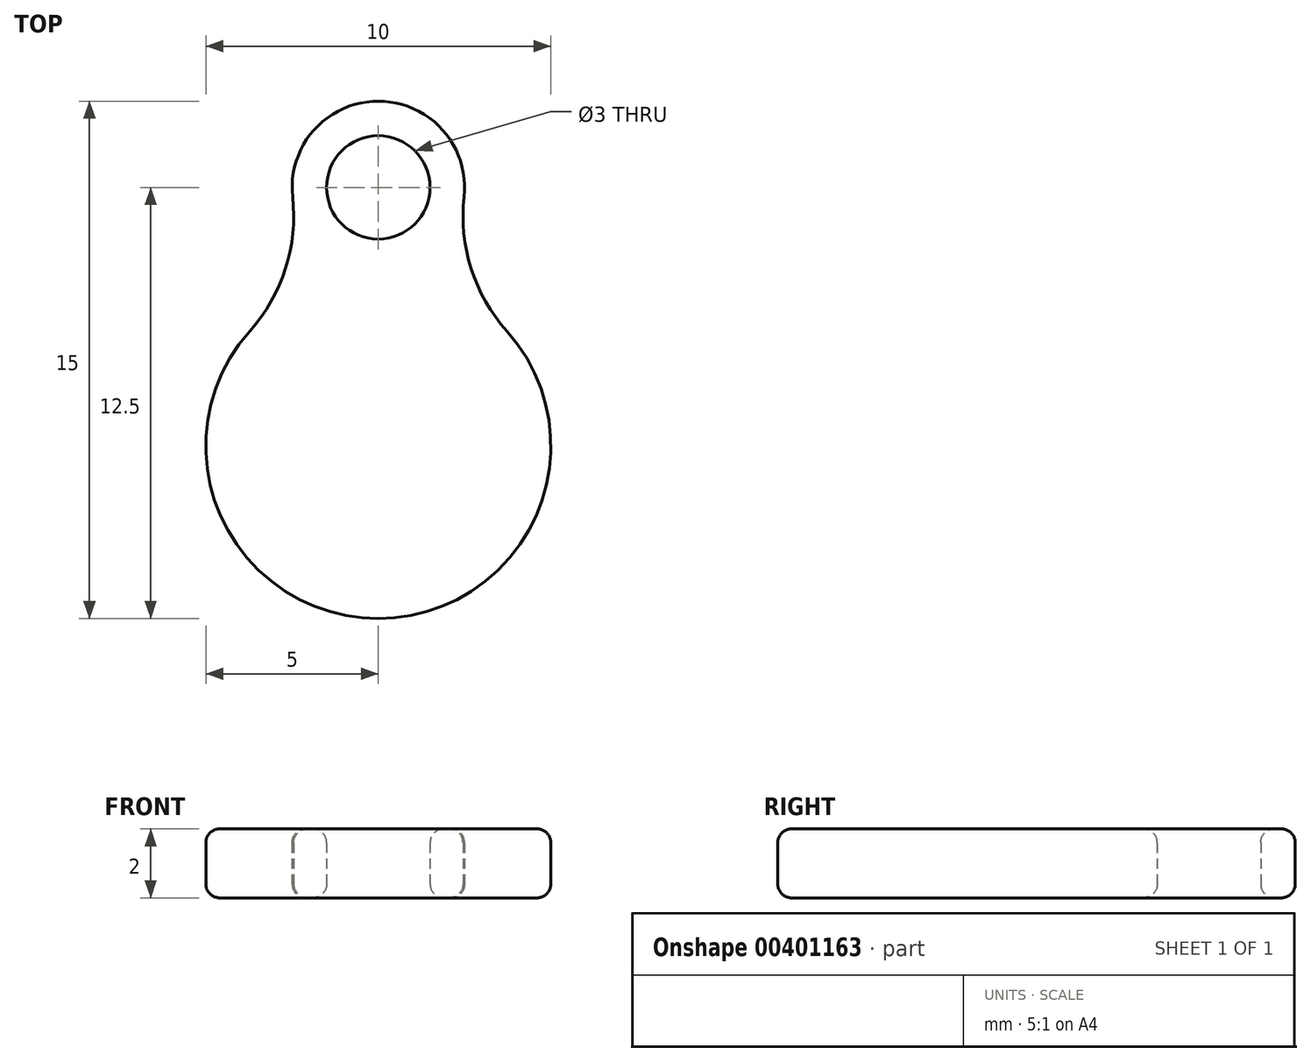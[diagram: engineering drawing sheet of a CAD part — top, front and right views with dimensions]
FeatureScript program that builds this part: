
annotation { "Feature Type Name" : "Feature", "Feature Type Description" : "" }
export const myFeature = defineFeature(function(context is Context, id is Id, definition is map)
    precondition{}
    {
        {
            var Q0;
            Q0=qCreatedBy(makeId("Top.planeOp"),FACE);
            var sketch = newSketch(context, id + "F0", { "sketchPlane" : qUnion([Q0])});
            skCircle(sketch, "E0", {"center": v(0, 0) * mm, "radius": 5 * mm});
            skCircle(sketch, "E1", {"center": v(0, 7.5) * mm, "radius": 2.5 * mm});
            skArc(sketch, "E2", {"start": v(-2.48, 7.22) * mm, "mid": v(-2.7, 5.15) * mm, "end": v(-3.73, 3.33) * mm});
            skLineSegment(sketch, "E3", {"start": v(0, 7.5) * mm, "end": v(0, 0) * mm, "construction": true});
            skArc(sketch, "E4.MirrorCS", {"start": v(2.48, 7.22) * mm, "mid": v(2.7, 5.15) * mm, "end": v(3.73, 3.33) * mm});
            skCircle(sketch, "E5", {"center": v(0, 7.5) * mm, "radius": 1.5 * mm});
            skSolve(sketch);
        }
        {
            var Q0;
            Q0 = qSketchRegion(id + "F0", true);
            extrude(context, id + "F1", {"entities" : qUnion([Q0]), "depth" : 2 * mm});
        }
        {
            var Q0;
            Q0=makeQuery(id+"F1.opExtrude","CAP_FACE",FACE,{"disambiguationData":[OSD([sQuery(id+"F0.wireOp",EDGE,"E0"),sQuery(id+"F0.wireOp",EDGE,"E1"),sQuery(id+"F0.wireOp",EDGE,"E2"),sQuery(id+"F0.wireOp",EDGE,"E4.MirrorCS"),sQuery(id+"F0.wireOp",EDGE,"E5")])],"isStart":true});
            var Q1;
            Q1=makeQuery(id+"F1.opExtrude","CAP_FACE",FACE,{"disambiguationData":[OSD([sQuery(id+"F0.wireOp",EDGE,"E0"),sQuery(id+"F0.wireOp",EDGE,"E1"),sQuery(id+"F0.wireOp",EDGE,"E2"),sQuery(id+"F0.wireOp",EDGE,"E4.MirrorCS"),sQuery(id+"F0.wireOp",EDGE,"E5")])],"isStart":false});
            fillet(context, id + "F2", {"entities" : qUnion([Q0, Q1]), "radius" : 0.4 * mm, "allowEdgeOverflow" : false});
        }
    });
